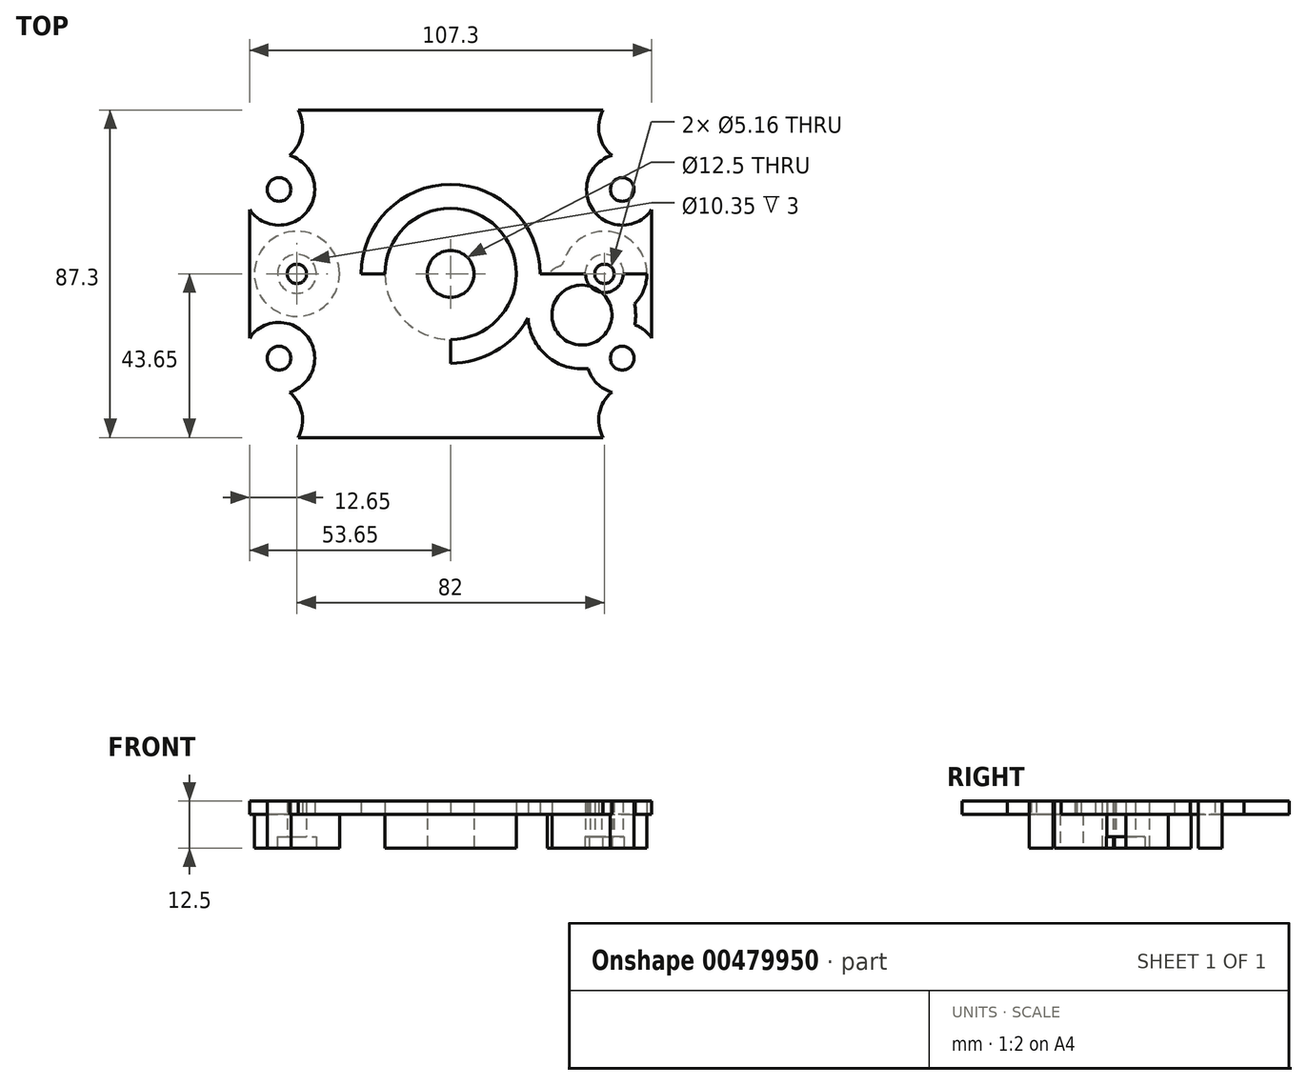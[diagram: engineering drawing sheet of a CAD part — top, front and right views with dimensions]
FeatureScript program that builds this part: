
annotation { "Feature Type Name" : "Feature", "Feature Type Description" : "" }
export const myFeature = defineFeature(function(context is Context, id is Id, definition is map)
    precondition{}
    {
        {
            var Q0;
            Q0=qCreatedBy(makeId("Top.planeOp"),FACE);
            var sketch = newSketch(context, id + "F0", { "sketchPlane" : qUnion([Q0])});
            skLineSegment(sketch, "E0", {"start": v(0, 60) * mm, "end": v(0, -60) * mm});
            skLineSegment(sketch, "E1", {"start": v(-70, 0) * mm, "end": v(70, 0) * mm});
            skLineSegment(sketch, "E2", {"start": v(-60, 50) * mm, "end": v(-60, -50) * mm});
            skLineSegment(sketch, "E3", {"start": v(60, 50) * mm, "end": v(60, -50) * mm});
            skLineSegment(sketch, "E4", {"start": v(-60, 50) * mm, "end": v(60, 50) * mm});
            skLineSegment(sketch, "E5", {"start": v(-60, -50) * mm, "end": v(60, -50) * mm});
            skCircle(sketch, "E6", {"center": v(0, 0) * mm, "radius": 6.25 * mm});
            skCircle(sketch, "E7", {"center": v(-45.77, 22.5) * mm, "radius": 3.17 * mm});
            skCircle(sketch, "E8", {"center": v(-45.77, -22.5) * mm, "radius": 3.17 * mm});
            skCircle(sketch, "E9", {"center": v(45.77, -22.5) * mm, "radius": 3.17 * mm});
            skCircle(sketch, "E10", {"center": v(45.77, 22.5) * mm, "radius": 3.17 * mm});
            skCircle(sketch, "E11", {"center": v(-41, 0) * mm, "radius": 2.58 * mm});
            skCircle(sketch, "E12", {"center": v(41, 0) * mm, "radius": 2.58 * mm});
            skCircle(sketch, "E13", {"center": v(-41, 0) * mm, "radius": 5 * mm});
            skCircle(sketch, "E14", {"center": v(41, 0) * mm, "radius": 5 * mm});
            skCircle(sketch, "E15", {"center": v(-49, -39) * mm, "radius": 3.17 * mm});
            skCircle(sketch, "E16", {"center": v(49, -39) * mm, "radius": 3.17 * mm});
            skCircle(sketch, "E17", {"center": v(-49, 39) * mm, "radius": 3.17 * mm});
            skCircle(sketch, "E18", {"center": v(49, 39) * mm, "radius": 3.17 * mm});
            skCircle(sketch, "E19", {"center": v(0, 0) * mm, "radius": 17.5 * mm});
            skCircle(sketch, "E20", {"center": v(35, -11) * mm, "radius": 8 * mm});
            skCircle(sketch, "E21", {"center": v(35, -11) * mm, "radius": 3.17 * mm});
            skArc(sketch, "E22", {"start": v(-42.99, 31.61) * mm, "mid": v(-39.64, 37.21) * mm, "end": v(-40.69, 43.65) * mm});
            skArc(sketch, "E23", {"start": v(40.69, 43.65) * mm, "mid": v(39.64, 37.21) * mm, "end": v(42.99, 31.61) * mm});
            skArc(sketch, "E24", {"start": v(42.99, 31.61) * mm, "mid": v(38.1, 16.85) * mm, "end": v(53.65, 17.15) * mm});
            skArc(sketch, "E25", {"start": v(49.04, -8.02) * mm, "mid": v(46.43, 9.96) * mm, "end": v(29.91, 2.42) * mm});
            skArc(sketch, "E26", {"start": v(49.12, -13.58) * mm, "mid": v(49.35, -10.8) * mm, "end": v(49.04, -8.02) * mm});
            skArc(sketch, "E27", {"start": v(53.65, -17.15) * mm, "mid": v(51.66, -15.02) * mm, "end": v(49.12, -13.58) * mm});
            skArc(sketch, "E28", {"start": v(42.99, -31.61) * mm, "mid": v(39.64, -37.21) * mm, "end": v(40.69, -43.65) * mm});
            skCircle(sketch, "E29", {"center": v(-41, 0) * mm, "radius": 11.35 * mm});
            skArc(sketch, "E30", {"start": v(-53.65, 17.15) * mm, "mid": v(-38.1, 16.85) * mm, "end": v(-42.99, 31.61) * mm});
            skArc(sketch, "E31", {"start": v(-42.99, -31.61) * mm, "mid": v(-38.1, -16.85) * mm, "end": v(-53.65, -17.15) * mm});
            skArc(sketch, "E32", {"start": v(-40.69, -43.65) * mm, "mid": v(-39.64, -37.21) * mm, "end": v(-42.99, -31.61) * mm});
            skArc(sketch, "E33", {"start": v(23.76, -2.08) * mm, "mid": v(-22.75, 7.15) * mm, "end": v(20.68, -11.89) * mm});
            skLineSegment(sketch, "E34", {"start": v(53.65, 17.15) * mm, "end": v(53.65, -17.15) * mm});
            skLineSegment(sketch, "E35", {"start": v(-40.69, -43.65) * mm, "end": v(40.69, -43.65) * mm});
            skLineSegment(sketch, "E36", {"start": v(-40.69, 43.65) * mm, "end": v(40.69, 43.65) * mm});
            skLineSegment(sketch, "E37", {"start": v(-53.65, 17.15) * mm, "end": v(-53.65, -17.15) * mm});
            skArc(sketch, "E38", {"start": v(20.68, -11.89) * mm, "mid": v(25.79, -22) * mm, "end": v(36.65, -25.25) * mm});
            skArc(sketch, "E39", {"start": v(29.91, 2.42) * mm, "mid": v(26.53, 0.58) * mm, "end": v(23.76, -2.08) * mm});
            skArc(sketch, "E40", {"start": v(36.65, -25.25) * mm, "mid": v(39.02, -29.23) * mm, "end": v(42.99, -31.61) * mm});
            skSolve(sketch);
        }
        {
            var Q0;
            {var subQ0=sQuery(id+"F0.wireOp",EDGE,"E22");Q0=makeQuery(id+"F0.imprint","IMPRINT",FACE,{"disambiguationData":[TD([[makeQuery(id+"F0.imprint","IMPRINT",EDGE,{"derivedFrom":subQ0}),-1.0]])]});}
            var Q1;
            Q1=makeQuery(id+"F0.imprint","IMPRINT",FACE,{"disambiguationData":[TD([[makeQuery(id+"F0.imprint","IMPRINT",EDGE,{"derivedFrom":sQuery(id+"F0.wireOp",EDGE,"E7")}),1.0]])]});
            var Q2;
            Q2=makeQuery(id+"F0.imprint","IMPRINT",FACE,{"disambiguationData":[TD([[makeQuery(id+"F0.imprint","IMPRINT",EDGE,{"derivedFrom":sQuery(id+"F0.wireOp",EDGE,"E10")}),1.0]])]});
            var Q3;
            {var subQ0=sQuery(id+"F0.wireOp",EDGE,"E23");Q3=makeQuery(id+"F0.imprint","IMPRINT",FACE,{"disambiguationData":[TD([[makeQuery(id+"F0.imprint","IMPRINT",EDGE,{"derivedFrom":subQ0}),-1.0]])]});}
            var Q4;
            {var subQ8=sQuery(id+"F0.wireOp",EDGE,"E31");Q4=makeQuery(id+"F0.imprint","IMPRINT",FACE,{"disambiguationData":[TD([[makeQuery(id+"F0.imprint","IMPRINT",EDGE,{"derivedFrom":subQ8}),-1.0]])]});}
            var Q5;
            Q5=makeQuery(id+"F0.imprint","IMPRINT",FACE,{"disambiguationData":[TD([[makeQuery(id+"F0.imprint","IMPRINT",EDGE,{"derivedFrom":sQuery(id+"F0.wireOp",EDGE,"E8")}),1.0]])]});
            var Q6;
            Q6=makeQuery(id+"F0.imprint","IMPRINT",FACE,{"disambiguationData":[TD([[makeQuery(id+"F0.imprint","IMPRINT",EDGE,{"derivedFrom":sQuery(id+"F0.wireOp",EDGE,"E9")}),1.0]])]});
            var Q7;
            {var subQ0=sQuery(id+"F0.wireOp",EDGE,"E33");var subQ1=sQuery(id+"F0.wireOp",EDGE,"E0");var subQ2=makeQuery(id+"F0.imprint","INTERSECT",VERTEX,{"disambiguationData":[OD(0.0)],"derivedFrom":[subQ1,subQ0]});Q7=makeQuery(id+"F0.imprint","IMPRINT",FACE,{"disambiguationData":[TD([[makeQuery(id+"F0.imprint","IMPRINT",EDGE,{"disambiguationData":[TD([[subQ2,-1.0]])],"derivedFrom":subQ1}),1.0]])]});}
            var Q8;
            {var subQ0=sQuery(id+"F0.wireOp",EDGE,"E19");var subQ1=sQuery(id+"F0.wireOp",EDGE,"E0");var subQ2=makeQuery(id+"F0.imprint","INTERSECT",VERTEX,{"disambiguationData":[OD(0.0)],"derivedFrom":[subQ1,subQ0]});Q8=makeQuery(id+"F0.imprint","IMPRINT",FACE,{"disambiguationData":[TD([[makeQuery(id+"F0.imprint","IMPRINT",EDGE,{"disambiguationData":[TD([[subQ2,-1.0]])],"derivedFrom":subQ1}),1.0]])]});}
            var Q9;
            {var subQ0=sQuery(id+"F0.wireOp",EDGE,"E19");var subQ1=sQuery(id+"F0.wireOp",EDGE,"E0");var subQ2=makeQuery(id+"F0.imprint","INTERSECT",VERTEX,{"disambiguationData":[OD(0.0)],"derivedFrom":[subQ1,subQ0]});Q9=makeQuery(id+"F0.imprint","IMPRINT",FACE,{"disambiguationData":[TD([[makeQuery(id+"F0.imprint","IMPRINT",EDGE,{"disambiguationData":[TD([[subQ2,-1.0]])],"derivedFrom":subQ1}),-1.0]])]});}
            var Q10;
            {var subQ0=sQuery(id+"F0.wireOp",EDGE,"E6");var subQ1=sQuery(id+"F0.wireOp",EDGE,"E0");var subQ2=makeQuery(id+"F0.imprint","INTERSECT",VERTEX,{"disambiguationData":[OD(1.0)],"derivedFrom":[subQ1,subQ0]});Q10=makeQuery(id+"F0.imprint","IMPRINT",FACE,{"disambiguationData":[TD([[makeQuery(id+"F0.imprint","IMPRINT",EDGE,{"disambiguationData":[TD([[subQ2,-1.0]])],"derivedFrom":subQ1}),-1.0]])]});}
            var Q11;
            {var subQ0=sQuery(id+"F0.wireOp",EDGE,"E6");var subQ1=sQuery(id+"F0.wireOp",EDGE,"E0");var subQ2=makeQuery(id+"F0.imprint","INTERSECT",VERTEX,{"disambiguationData":[OD(1.0)],"derivedFrom":[subQ1,subQ0]});Q11=makeQuery(id+"F0.imprint","IMPRINT",FACE,{"disambiguationData":[TD([[makeQuery(id+"F0.imprint","IMPRINT",EDGE,{"disambiguationData":[TD([[subQ2,-1.0]])],"derivedFrom":subQ1}),1.0]])]});}
            var Q12;
            {var subQ1=sQuery(id+"F0.wireOp",EDGE,"E28");Q12=makeQuery(id+"F0.imprint","IMPRINT",FACE,{"disambiguationData":[TD([[makeQuery(id+"F0.imprint","IMPRINT",EDGE,{"derivedFrom":subQ1}),-1.0]])]});}
            var Q13;
            {var subQ0=sQuery(id+"F0.wireOp",EDGE,"E19");var subQ1=sQuery(id+"F0.wireOp",EDGE,"E0");var subQ2=makeQuery(id+"F0.imprint","INTERSECT",VERTEX,{"disambiguationData":[OD(1.0)],"derivedFrom":[subQ1,subQ0]});Q13=makeQuery(id+"F0.imprint","IMPRINT",FACE,{"disambiguationData":[TD([[makeQuery(id+"F0.imprint","IMPRINT",EDGE,{"disambiguationData":[TD([[subQ2,-1.0]])],"derivedFrom":subQ1}),-1.0]])]});}
            var Q14;
            {var subQ0=sQuery(id+"F0.wireOp",EDGE,"E33");var subQ1=sQuery(id+"F0.wireOp",EDGE,"E0");var subQ2=makeQuery(id+"F0.imprint","INTERSECT",VERTEX,{"disambiguationData":[OD(0.0)],"derivedFrom":[subQ1,subQ0]});Q14=makeQuery(id+"F0.imprint","IMPRINT",FACE,{"disambiguationData":[TD([[makeQuery(id+"F0.imprint","IMPRINT",EDGE,{"disambiguationData":[TD([[subQ2,-1.0]])],"derivedFrom":subQ1}),-1.0]])]});}
            var Q15;
            {var subQ0=sQuery(id+"F0.wireOp",EDGE,"E13");var subQ1=sQuery(id+"F0.wireOp",EDGE,"E1");var subQ2=makeQuery(id+"F0.imprint","INTERSECT",VERTEX,{"disambiguationData":[OD(0.0)],"derivedFrom":[subQ1,subQ0]});Q15=makeQuery(id+"F0.imprint","IMPRINT",FACE,{"disambiguationData":[TD([[makeQuery(id+"F0.imprint","IMPRINT",EDGE,{"disambiguationData":[TD([[subQ2,-1.0]])],"derivedFrom":subQ1}),1.0]])]});}
            var Q16;
            {var subQ0=sQuery(id+"F0.wireOp",EDGE,"E13");var subQ1=sQuery(id+"F0.wireOp",EDGE,"E1");var subQ2=makeQuery(id+"F0.imprint","INTERSECT",VERTEX,{"disambiguationData":[OD(0.0)],"derivedFrom":[subQ1,subQ0]});Q16=makeQuery(id+"F0.imprint","IMPRINT",FACE,{"disambiguationData":[TD([[makeQuery(id+"F0.imprint","IMPRINT",EDGE,{"disambiguationData":[TD([[subQ2,-1.0]])],"derivedFrom":subQ1}),-1.0]])]});}
            var Q17;
            {var subQ0=sQuery(id+"F0.wireOp",EDGE,"E29");var subQ1=sQuery(id+"F0.wireOp",EDGE,"E1");var subQ2=makeQuery(id+"F0.imprint","INTERSECT",VERTEX,{"disambiguationData":[OD(0.0)],"derivedFrom":[subQ1,subQ0]});Q17=makeQuery(id+"F0.imprint","IMPRINT",FACE,{"disambiguationData":[TD([[makeQuery(id+"F0.imprint","IMPRINT",EDGE,{"disambiguationData":[TD([[subQ2,-1.0]])],"derivedFrom":subQ1}),1.0]])]});}
            var Q18;
            {var subQ0=sQuery(id+"F0.wireOp",EDGE,"E29");var subQ1=sQuery(id+"F0.wireOp",EDGE,"E1");var subQ2=makeQuery(id+"F0.imprint","INTERSECT",VERTEX,{"disambiguationData":[OD(0.0)],"derivedFrom":[subQ1,subQ0]});Q18=makeQuery(id+"F0.imprint","IMPRINT",FACE,{"disambiguationData":[TD([[makeQuery(id+"F0.imprint","IMPRINT",EDGE,{"disambiguationData":[TD([[subQ2,-1.0]])],"derivedFrom":subQ1}),-1.0]])]});}
            var Q19;
            {var subQ0=sQuery(id+"F0.wireOp",EDGE,"E26");Q19=makeQuery(id+"F0.imprint","IMPRINT",FACE,{"disambiguationData":[TD([[makeQuery(id+"F0.imprint","IMPRINT",EDGE,{"derivedFrom":subQ0}),-1.0]])]});}
            var Q20;
            {var subQ1=sQuery(id+"F0.wireOp",EDGE,"E1");var subQ3=sQuery(id+"F0.wireOp",EDGE,"E39");var subQ8=makeQuery(id+"F0.imprint","INTERSECT",VERTEX,{"derivedFrom":[subQ1,subQ3]});Q20=makeQuery(id+"F0.imprint","IMPRINT",FACE,{"disambiguationData":[TD([[makeQuery(id+"F0.imprint","IMPRINT",EDGE,{"disambiguationData":[TD([[subQ8,-1.0]])],"derivedFrom":subQ1}),1.0]])]});}
            var Q21;
            {var subQ0=sQuery(id+"F0.wireOp",EDGE,"E14");var subQ1=sQuery(id+"F0.wireOp",EDGE,"E1");var subQ2=makeQuery(id+"F0.imprint","INTERSECT",VERTEX,{"disambiguationData":[OD(0.0)],"derivedFrom":[subQ1,subQ0]});Q21=makeQuery(id+"F0.imprint","IMPRINT",FACE,{"disambiguationData":[TD([[makeQuery(id+"F0.imprint","IMPRINT",EDGE,{"disambiguationData":[TD([[subQ2,-1.0]])],"derivedFrom":subQ1}),1.0]])]});}
            var Q22;
            {var subQ0=sQuery(id+"F0.wireOp",EDGE,"E14");var subQ1=sQuery(id+"F0.wireOp",EDGE,"E1");var subQ8=makeQuery(id+"F0.imprint","INTERSECT",VERTEX,{"disambiguationData":[OD(0.0)],"derivedFrom":[subQ1,subQ0]});Q22=makeQuery(id+"F0.imprint","IMPRINT",FACE,{"disambiguationData":[TD([[makeQuery(id+"F0.imprint","IMPRINT",EDGE,{"disambiguationData":[TD([[subQ8,-1.0]])],"derivedFrom":subQ1}),-1.0]])]});}
            var Q23;
            Q23=makeQuery(id+"F0.imprint","IMPRINT",FACE,{"disambiguationData":[TD([[makeQuery(id+"F0.imprint","IMPRINT",EDGE,{"derivedFrom":sQuery(id+"F0.wireOp",EDGE,"E21")}),1.0]])]});
            var Q24;
            {var subQ0=sQuery(id+"F0.wireOp",EDGE,"E20");var subQ1=sQuery(id+"F0.wireOp",EDGE,"E14");var subQ2=makeQuery(id+"F0.imprint","INTERSECT",VERTEX,{"disambiguationData":[OD(0.0)],"derivedFrom":[subQ1,subQ0]});Q24=makeQuery(id+"F0.imprint","IMPRINT",FACE,{"disambiguationData":[TD([[makeQuery(id+"F0.imprint","IMPRINT",EDGE,{"disambiguationData":[TD([[subQ2,-1.0]])],"derivedFrom":subQ1}),-1.0]])]});}
            var Q25;
            {var subQ0=sQuery(id+"F0.wireOp",EDGE,"E33");var subQ1=sQuery(id+"F0.wireOp",EDGE,"E1");var subQ2=makeQuery(id+"F0.imprint","INTERSECT",VERTEX,{"disambiguationData":[OD(1.0)],"derivedFrom":[subQ1,subQ0]});Q25=makeQuery(id+"F0.imprint","IMPRINT",FACE,{"disambiguationData":[TD([[makeQuery(id+"F0.imprint","IMPRINT",EDGE,{"disambiguationData":[TD([[subQ2,-1.0]])],"derivedFrom":subQ1}),-1.0]])]});}
            extrude(context, id + "F1", {"entities" : qUnion([Q0, Q1, Q2, Q3, Q4, Q5, Q6, Q7, Q8, Q9, Q10, Q11, Q12, Q13, Q14, Q15, Q16, Q17, Q18, Q19, Q20, Q21, Q22, Q23, Q24, Q25]), "depth" : 12.5 * mm});
        }
        {
            var Q0;
            Q0=qCreatedBy(makeId("Top.planeOp"),FACE);
            var sketch = newSketch(context, id + "F2", { "sketchPlane" : qUnion([Q0])});
            skLineSegment(sketch, "E41", {"start": v(0, 60) * mm, "end": v(0, -60) * mm});
            skLineSegment(sketch, "E42", {"start": v(-70, 0) * mm, "end": v(70, 0) * mm});
            skLineSegment(sketch, "E43", {"start": v(-60, 50) * mm, "end": v(-60, -50) * mm});
            skLineSegment(sketch, "E44", {"start": v(60, 50) * mm, "end": v(60, -50) * mm});
            skLineSegment(sketch, "E45", {"start": v(-60, 50) * mm, "end": v(60, 50) * mm});
            skLineSegment(sketch, "E46", {"start": v(-60, -50) * mm, "end": v(60, -50) * mm});
            skCircle(sketch, "E47", {"center": v(0, 0) * mm, "radius": 6.25 * mm});
            skCircle(sketch, "E48", {"center": v(-45.77, 22.5) * mm, "radius": 3.17 * mm});
            skCircle(sketch, "E49", {"center": v(-45.77, -22.5) * mm, "radius": 3.17 * mm});
            skCircle(sketch, "E50", {"center": v(45.77, -22.5) * mm, "radius": 3.17 * mm});
            skCircle(sketch, "E51", {"center": v(45.77, 22.5) * mm, "radius": 3.17 * mm});
            skCircle(sketch, "E52", {"center": v(-41, 0) * mm, "radius": 2.58 * mm});
            skCircle(sketch, "E53", {"center": v(41, 0) * mm, "radius": 2.58 * mm});
            skCircle(sketch, "E54", {"center": v(-41, 0) * mm, "radius": 5 * mm});
            skCircle(sketch, "E55", {"center": v(41, 0) * mm, "radius": 5 * mm});
            skCircle(sketch, "E56", {"center": v(-49, -39) * mm, "radius": 3.17 * mm});
            skCircle(sketch, "E57", {"center": v(49, -39) * mm, "radius": 3.17 * mm});
            skCircle(sketch, "E58", {"center": v(-49, 39) * mm, "radius": 3.17 * mm});
            skCircle(sketch, "E59", {"center": v(49, 39) * mm, "radius": 3.17 * mm});
            skCircle(sketch, "E60", {"center": v(0, 0) * mm, "radius": 17.5 * mm});
            skCircle(sketch, "E61", {"center": v(35, -11) * mm, "radius": 8 * mm});
            skCircle(sketch, "E62", {"center": v(35, -11) * mm, "radius": 3.17 * mm});
            skArc(sketch, "E63", {"start": v(-42.99, 31.61) * mm, "mid": v(-39.64, 37.21) * mm, "end": v(-40.69, 43.65) * mm});
            skArc(sketch, "E64", {"start": v(40.69, 43.65) * mm, "mid": v(39.64, 37.21) * mm, "end": v(42.99, 31.61) * mm});
            skArc(sketch, "E65", {"start": v(42.99, 31.61) * mm, "mid": v(38.1, 16.85) * mm, "end": v(53.65, 17.15) * mm});
            skArc(sketch, "E66", {"start": v(49.04, -8.02) * mm, "mid": v(46.43, 9.96) * mm, "end": v(29.91, 2.42) * mm});
            skArc(sketch, "E67", {"start": v(49.12, -13.58) * mm, "mid": v(49.35, -10.8) * mm, "end": v(49.04, -8.02) * mm});
            skArc(sketch, "E68", {"start": v(53.65, -17.15) * mm, "mid": v(51.66, -15.02) * mm, "end": v(49.12, -13.58) * mm});
            skArc(sketch, "E69", {"start": v(42.99, -31.61) * mm, "mid": v(39.64, -37.21) * mm, "end": v(40.69, -43.65) * mm});
            skCircle(sketch, "E70", {"center": v(-41, 0) * mm, "radius": 11.35 * mm});
            skArc(sketch, "E71", {"start": v(-53.65, 17.15) * mm, "mid": v(-38.1, 16.85) * mm, "end": v(-42.99, 31.61) * mm});
            skArc(sketch, "E72", {"start": v(-42.99, -31.61) * mm, "mid": v(-38.1, -16.85) * mm, "end": v(-53.65, -17.15) * mm});
            skArc(sketch, "E73", {"start": v(-40.69, -43.65) * mm, "mid": v(-39.64, -37.21) * mm, "end": v(-42.99, -31.61) * mm});
            skArc(sketch, "E74", {"start": v(23.76, -2.08) * mm, "mid": v(-22.75, 7.15) * mm, "end": v(20.68, -11.89) * mm});
            skLineSegment(sketch, "E75", {"start": v(53.65, 17.15) * mm, "end": v(53.65, -17.15) * mm});
            skLineSegment(sketch, "E76", {"start": v(-40.69, -43.65) * mm, "end": v(40.69, -43.65) * mm});
            skLineSegment(sketch, "E77", {"start": v(-40.69, 43.65) * mm, "end": v(40.69, 43.65) * mm});
            skLineSegment(sketch, "E78", {"start": v(-53.65, 17.15) * mm, "end": v(-53.65, -17.15) * mm});
            skArc(sketch, "E79", {"start": v(20.68, -11.89) * mm, "mid": v(25.79, -22) * mm, "end": v(36.65, -25.25) * mm});
            skArc(sketch, "E80", {"start": v(29.91, 2.42) * mm, "mid": v(26.53, 0.58) * mm, "end": v(23.76, -2.08) * mm});
            skArc(sketch, "E81", {"start": v(36.65, -25.25) * mm, "mid": v(39.02, -29.23) * mm, "end": v(42.99, -31.61) * mm});
            skSolve(sketch);
        }
        {
            var Q0;
            {var subQ0=sQuery(id+"F2.wireOp",EDGE,"E63");Q0=makeQuery(id+"F2.imprint","IMPRINT",FACE,{"disambiguationData":[TD([[makeQuery(id+"F2.imprint","IMPRINT",EDGE,{"derivedFrom":subQ0}),-1.0]])]});}
            var Q1;
            {var subQ0=sQuery(id+"F2.wireOp",EDGE,"E64");Q1=makeQuery(id+"F2.imprint","IMPRINT",FACE,{"disambiguationData":[TD([[makeQuery(id+"F2.imprint","IMPRINT",EDGE,{"derivedFrom":subQ0}),-1.0]])]});}
            var Q2;
            {var subQ1=sQuery(id+"F2.wireOp",EDGE,"E69");Q2=makeQuery(id+"F2.imprint","IMPRINT",FACE,{"disambiguationData":[TD([[makeQuery(id+"F2.imprint","IMPRINT",EDGE,{"derivedFrom":subQ1}),-1.0]])]});}
            var Q3;
            {var subQ8=sQuery(id+"F2.wireOp",EDGE,"E72");Q3=makeQuery(id+"F2.imprint","IMPRINT",FACE,{"disambiguationData":[TD([[makeQuery(id+"F2.imprint","IMPRINT",EDGE,{"derivedFrom":subQ8}),-1.0]])]});}
            var Q4;
            {var subQ0=sQuery(id+"F2.wireOp",EDGE,"E67");Q4=makeQuery(id+"F2.imprint","IMPRINT",FACE,{"disambiguationData":[TD([[makeQuery(id+"F2.imprint","IMPRINT",EDGE,{"derivedFrom":subQ0}),-1.0]])]});}
            var Q5;
            {var subQ0=sQuery(id+"F2.wireOp",EDGE,"E74");var subQ1=sQuery(id+"F2.wireOp",EDGE,"E42");var subQ2=makeQuery(id+"F2.imprint","INTERSECT",VERTEX,{"disambiguationData":[OD(1.0)],"derivedFrom":[subQ1,subQ0]});Q5=makeQuery(id+"F2.imprint","IMPRINT",FACE,{"disambiguationData":[TD([[makeQuery(id+"F2.imprint","IMPRINT",EDGE,{"disambiguationData":[TD([[subQ2,-1.0]])],"derivedFrom":subQ1}),-1.0]])]});}
            extrude(context, id + "F3", {"entities" : qUnion([Q0, Q1, Q2, Q3, Q4, Q5]), "operationType" : NewBodyOperationType.REMOVE, "depth" : 9 * mm});
        }
        {
            var Q0;
            {var subQ0=sQuery(id+"F0.wireOp",EDGE,"E11");Q0=makeQuery(id+"F3.boolean.opBoolean","SPLIT",FACE,{"disambiguationData":[TD([makeQuery(id+"F1.opExtrude","SWEPT_FACE",FACE,{"disambiguationData":[OSD([subQ0])]})])],"derivedFrom":makeQuery(id+"F1.opExtrude","CAP_FACE",FACE,{"disambiguationData":[OSD([sQuery(id+"F0.wireOp",EDGE,"E2"),sQuery(id+"F0.wireOp",EDGE,"E3"),sQuery(id+"F0.wireOp",EDGE,"E4"),sQuery(id+"F0.wireOp",EDGE,"E5"),sQuery(id+"F0.wireOp",EDGE,"E6"),sQuery(id+"F0.wireOp",EDGE,"E7"),sQuery(id+"F0.wireOp",EDGE,"E8"),sQuery(id+"F0.wireOp",EDGE,"E9"),sQuery(id+"F0.wireOp",EDGE,"E10"),subQ0,sQuery(id+"F0.wireOp",EDGE,"E12"),sQuery(id+"F0.wireOp",EDGE,"E15"),sQuery(id+"F0.wireOp",EDGE,"E16"),sQuery(id+"F0.wireOp",EDGE,"E17"),sQuery(id+"F0.wireOp",EDGE,"E18"),sQuery(id+"F0.wireOp",EDGE,"E21")])],"isStart":true})});}
            var sketch = newSketch(context, id + "F4", { "sketchPlane" : qUnion([Q0])});
            skCircle(sketch, "E82", {"center": v(-41, 0) * mm, "radius": 5.17 * mm});
            skSolve(sketch);
        }
        {
            var Q0;
            {var subQ0=sQuery(id+"F0.wireOp",EDGE,"E21");var subQ1=sQuery(id+"F0.wireOp",EDGE,"E18");var subQ2=sQuery(id+"F0.wireOp",EDGE,"E17");var subQ3=sQuery(id+"F0.wireOp",EDGE,"E16");var subQ4=sQuery(id+"F0.wireOp",EDGE,"E15");var subQ5=sQuery(id+"F0.wireOp",EDGE,"E4");var subQ6=sQuery(id+"F0.wireOp",EDGE,"E3");var subQ7=sQuery(id+"F0.wireOp",EDGE,"E5");var subQ8=sQuery(id+"F0.wireOp",EDGE,"E2");var subQ9=sQuery(id+"F0.wireOp",EDGE,"E6");var subQ10=sQuery(id+"F0.wireOp",EDGE,"E7");var subQ11=sQuery(id+"F0.wireOp",EDGE,"E8");var subQ12=sQuery(id+"F0.wireOp",EDGE,"E9");var subQ13=sQuery(id+"F0.wireOp",EDGE,"E10");var subQ14=sQuery(id+"F0.wireOp",EDGE,"E12");Q0=makeQuery(id+"F3.boolean.opBoolean","SPLIT",FACE,{"disambiguationData":[TD([makeQuery(id+"F1.opExtrude","SWEPT_FACE",FACE,{"disambiguationData":[OSD([subQ8])]})])],"derivedFrom":makeQuery(id+"F1.opExtrude","CAP_FACE",FACE,{"disambiguationData":[OSD([subQ8,subQ6,subQ5,subQ7,subQ9,subQ10,subQ11,subQ12,subQ13,sQuery(id+"F0.wireOp",EDGE,"E11"),subQ14,subQ4,subQ3,subQ2,subQ1,subQ0])],"isStart":true})});}
            var sketch = newSketch(context, id + "F5", { "sketchPlane" : qUnion([Q0])});
            skCircle(sketch, "E83", {"center": v(41, 0) * mm, "radius": 5.17 * mm});
            skSolve(sketch);
        }
        {
            var Q0;
            Q0=makeQuery(id+"F4.imprint","IMPRINT",FACE,{"disambiguationData":[TD([[makeQuery(id+"F4.imprint","IMPRINT",EDGE,{"derivedFrom":sQuery(id+"F4.wireOp",EDGE,"E82")}),1.0]])]});
            extrude(context, id + "F6", {"entities" : qUnion([Q0]), "operationType" : NewBodyOperationType.REMOVE, "oppositeDirection" : true, "depth" : 3 * mm});
        }
        {
            var Q0;
            Q0=makeQuery(id+"F5.imprint","IMPRINT",FACE,{"disambiguationData":[TD([[makeQuery(id+"F5.imprint","IMPRINT",EDGE,{"derivedFrom":sQuery(id+"F5.wireOp",EDGE,"E83")}),1.0]])]});
            extrude(context, id + "F7", {"entities" : qUnion([Q0]), "operationType" : NewBodyOperationType.REMOVE, "oppositeDirection" : true, "depth" : 3 * mm});
        }
        {
            var Q0;
            Q0=makeQuery(id+"F3.boolean.opBoolean","COPY",EDGE,{"derivedFrom":makeQuery(id+"F3.opExtrude","SWEPT_EDGE",EDGE,{"disambiguationData":[OSD([sQuery(id+"F2.wireOp",EDGE,"E69"),sQuery(id+"F2.wireOp",EDGE,"E76")])]})});
            var Q1;
            Q1=makeQuery(id+"F3.boolean.opBoolean","COPY",EDGE,{"derivedFrom":makeQuery(id+"F3.opExtrude","SWEPT_EDGE",EDGE,{"disambiguationData":[OSD([sQuery(id+"F2.wireOp",EDGE,"E73"),sQuery(id+"F2.wireOp",EDGE,"E76")])]})});
            var Q2;
            Q2=makeQuery(id+"F3.boolean.opBoolean","COPY",EDGE,{"derivedFrom":makeQuery(id+"F3.opExtrude","SWEPT_EDGE",EDGE,{"disambiguationData":[OSD([sQuery(id+"F2.wireOp",EDGE,"E72"),sQuery(id+"F2.wireOp",EDGE,"E73")])]})});
            var Q3;
            Q3=makeQuery(id+"F3.boolean.opBoolean","COPY",EDGE,{"derivedFrom":makeQuery(id+"F3.opExtrude","SWEPT_EDGE",EDGE,{"disambiguationData":[OSD([sQuery(id+"F2.wireOp",EDGE,"E72"),sQuery(id+"F2.wireOp",EDGE,"E78")])]})});
            var Q4;
            Q4=makeQuery(id+"F3.boolean.opBoolean","COPY",EDGE,{"derivedFrom":makeQuery(id+"F3.opExtrude","SWEPT_EDGE",EDGE,{"disambiguationData":[OSD([sQuery(id+"F2.wireOp",EDGE,"E69"),sQuery(id+"F2.wireOp",EDGE,"E81")])]})});
            var Q5;
            Q5=makeQuery(id+"F3.boolean.opBoolean","COPY",EDGE,{"derivedFrom":makeQuery(id+"F3.opExtrude","SWEPT_EDGE",EDGE,{"disambiguationData":[OSD([sQuery(id+"F2.wireOp",EDGE,"E67"),sQuery(id+"F2.wireOp",EDGE,"E68")])]})});
            var Q6;
            Q6=makeQuery(id+"F3.boolean.opBoolean","COPY",EDGE,{"derivedFrom":makeQuery(id+"F3.opExtrude","SWEPT_EDGE",EDGE,{"disambiguationData":[OSD([sQuery(id+"F2.wireOp",EDGE,"E66"),sQuery(id+"F2.wireOp",EDGE,"E67")])]})});
            var Q7;
            Q7=makeQuery(id+"F3.boolean.opBoolean","COPY",EDGE,{"derivedFrom":makeQuery(id+"F3.opExtrude","SWEPT_EDGE",EDGE,{"disambiguationData":[OSD([sQuery(id+"F2.wireOp",EDGE,"E68"),sQuery(id+"F2.wireOp",EDGE,"E75")])]})});
            var Q8;
            Q8=makeQuery(id+"F3.boolean.opBoolean","COPY",EDGE,{"derivedFrom":makeQuery(id+"F3.opExtrude","SWEPT_EDGE",EDGE,{"disambiguationData":[OSD([sQuery(id+"F2.wireOp",EDGE,"E65"),sQuery(id+"F2.wireOp",EDGE,"E75")])]})});
            var Q9;
            Q9=makeQuery(id+"F3.boolean.opBoolean","COPY",EDGE,{"derivedFrom":makeQuery(id+"F3.opExtrude","SWEPT_EDGE",EDGE,{"disambiguationData":[OSD([sQuery(id+"F2.wireOp",EDGE,"E64"),sQuery(id+"F2.wireOp",EDGE,"E77")])]})});
            var Q10;
            Q10=makeQuery(id+"F3.boolean.opBoolean","COPY",EDGE,{"derivedFrom":makeQuery(id+"F3.opExtrude","SWEPT_EDGE",EDGE,{"disambiguationData":[OSD([sQuery(id+"F2.wireOp",EDGE,"E64"),sQuery(id+"F2.wireOp",EDGE,"E65")])]})});
            var Q11;
            Q11=makeQuery(id+"F3.boolean.opBoolean","COPY",EDGE,{"derivedFrom":makeQuery(id+"F3.opExtrude","SWEPT_EDGE",EDGE,{"disambiguationData":[OSD([sQuery(id+"F2.wireOp",EDGE,"E63"),sQuery(id+"F2.wireOp",EDGE,"E71")])]})});
            var Q12;
            Q12=makeQuery(id+"F3.boolean.opBoolean","COPY",EDGE,{"derivedFrom":makeQuery(id+"F3.opExtrude","SWEPT_EDGE",EDGE,{"disambiguationData":[OSD([sQuery(id+"F2.wireOp",EDGE,"E63"),sQuery(id+"F2.wireOp",EDGE,"E77")])]})});
            var Q13;
            Q13=makeQuery(id+"F3.boolean.opBoolean","COPY",EDGE,{"derivedFrom":makeQuery(id+"F3.opExtrude","SWEPT_EDGE",EDGE,{"disambiguationData":[OSD([sQuery(id+"F2.wireOp",EDGE,"E71"),sQuery(id+"F2.wireOp",EDGE,"E78")])]})});
            var Q14;
            Q14=makeQuery(id+"F3.boolean.opBoolean","COPY",EDGE,{"derivedFrom":makeQuery(id+"F3.opExtrude","SWEPT_EDGE",EDGE,{"disambiguationData":[OSD([sQuery(id+"F2.wireOp",EDGE,"E66"),sQuery(id+"F2.wireOp",EDGE,"E80")])]})});
            var Q15;
            Q15=makeQuery(id+"F3.boolean.opBoolean","COPY",EDGE,{"derivedFrom":makeQuery(id+"F3.opExtrude","SWEPT_EDGE",EDGE,{"disambiguationData":[OSD([sQuery(id+"F2.wireOp",EDGE,"E74"),sQuery(id+"F2.wireOp",EDGE,"E80")])]})});
            var Q16;
            Q16=makeQuery(id+"F3.boolean.opBoolean","COPY",EDGE,{"derivedFrom":makeQuery(id+"F3.opExtrude","SWEPT_EDGE",EDGE,{"disambiguationData":[OSD([sQuery(id+"F2.wireOp",EDGE,"E74"),sQuery(id+"F2.wireOp",EDGE,"E79")])]})});
            var Q17;
            Q17=makeQuery(id+"F3.boolean.opBoolean","COPY",EDGE,{"derivedFrom":makeQuery(id+"F3.opExtrude","SWEPT_EDGE",EDGE,{"disambiguationData":[OSD([sQuery(id+"F2.wireOp",EDGE,"E79"),sQuery(id+"F2.wireOp",EDGE,"E81")])]})});
            fillet(context, id + "F8", {"entities" : qUnion([Q0, Q1, Q2, Q3, Q4, Q5, Q6, Q7, Q8, Q9, Q10, Q11, Q12, Q13, Q14, Q15, Q16, Q17]), "radius" : (25 / 16) * mm, "tangentPropagation" : true, "allowEdgeOverflow" : false});
        }
    });
